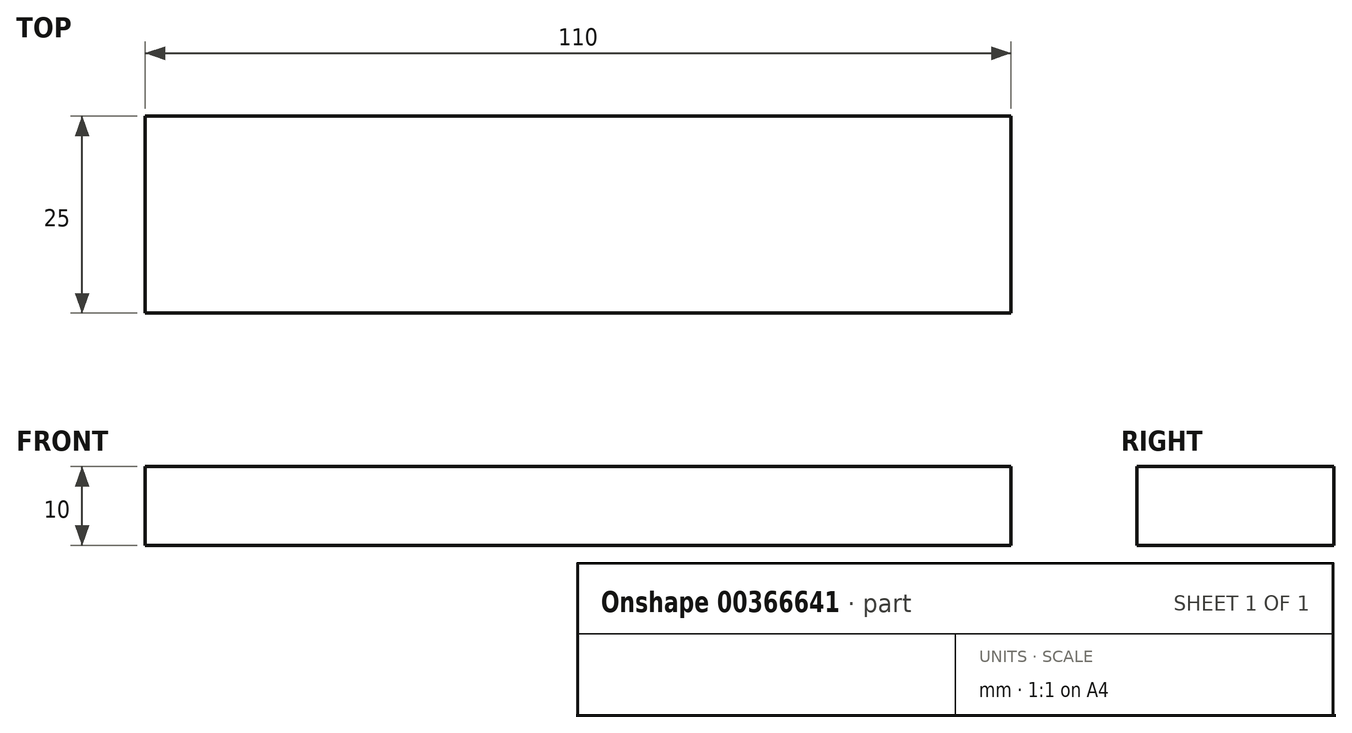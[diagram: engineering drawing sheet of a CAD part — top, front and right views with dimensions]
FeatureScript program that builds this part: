
annotation { "Feature Type Name" : "Feature", "Feature Type Description" : "" }
export const myFeature = defineFeature(function(context is Context, id is Id, definition is map)
    precondition{}
    {
        {
            var Q0;
            Q0=qCreatedBy(makeId("Top.planeOp"),FACE);
            var sketch = newSketch(context, id + "F0", { "sketchPlane" : qUnion([Q0])});
            skLineSegment(sketch, "E0.bottom", {"start": v(0, 0) * mm, "end": v(110, 0) * mm});
            skLineSegment(sketch, "E0.top", {"start": v(0, -25) * mm, "end": v(110, -25) * mm});
            skLineSegment(sketch, "E0.left", {"start": v(0, 0) * mm, "end": v(0, -25) * mm});
            skLineSegment(sketch, "E0.right", {"start": v(110, 0) * mm, "end": v(110, -25) * mm});
            skSolve(sketch);
        }
        {
            var Q0;
            Q0=makeQuery(id+"F0.imprint","IMPRINT",FACE,{"disambiguationData":[TD([[makeQuery(id+"F0.imprint","IMPRINT",EDGE,{"derivedFrom":sQuery(id+"F0.wireOp",EDGE,"E0.bottom")}),-1.0]])]});
            extrude(context, id + "F1", {"entities" : qUnion([Q0]), "depth" : 10 * mm});
        }
    });
